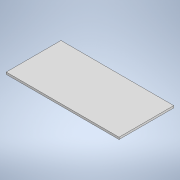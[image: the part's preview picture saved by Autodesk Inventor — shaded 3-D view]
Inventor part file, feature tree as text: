
AUTODESK INVENTOR PART (.ipt)
format: ipt  version: 2020 (Build 240168000, 168)  size: 92,672 bytes
history: native  units: mm
features: extrude x1, sketch x1
ambient origin geometry x8: Origin, YZ Plane, XZ Plane, XY Plane, X Axis, Y Axis, Z Axis, Center Point
bodies: Solide1 (feature_tree)
feature tree (2):
  extrude  "Extrusion1"  Depth=330.0mm
  sketch  "Esquisse1"
